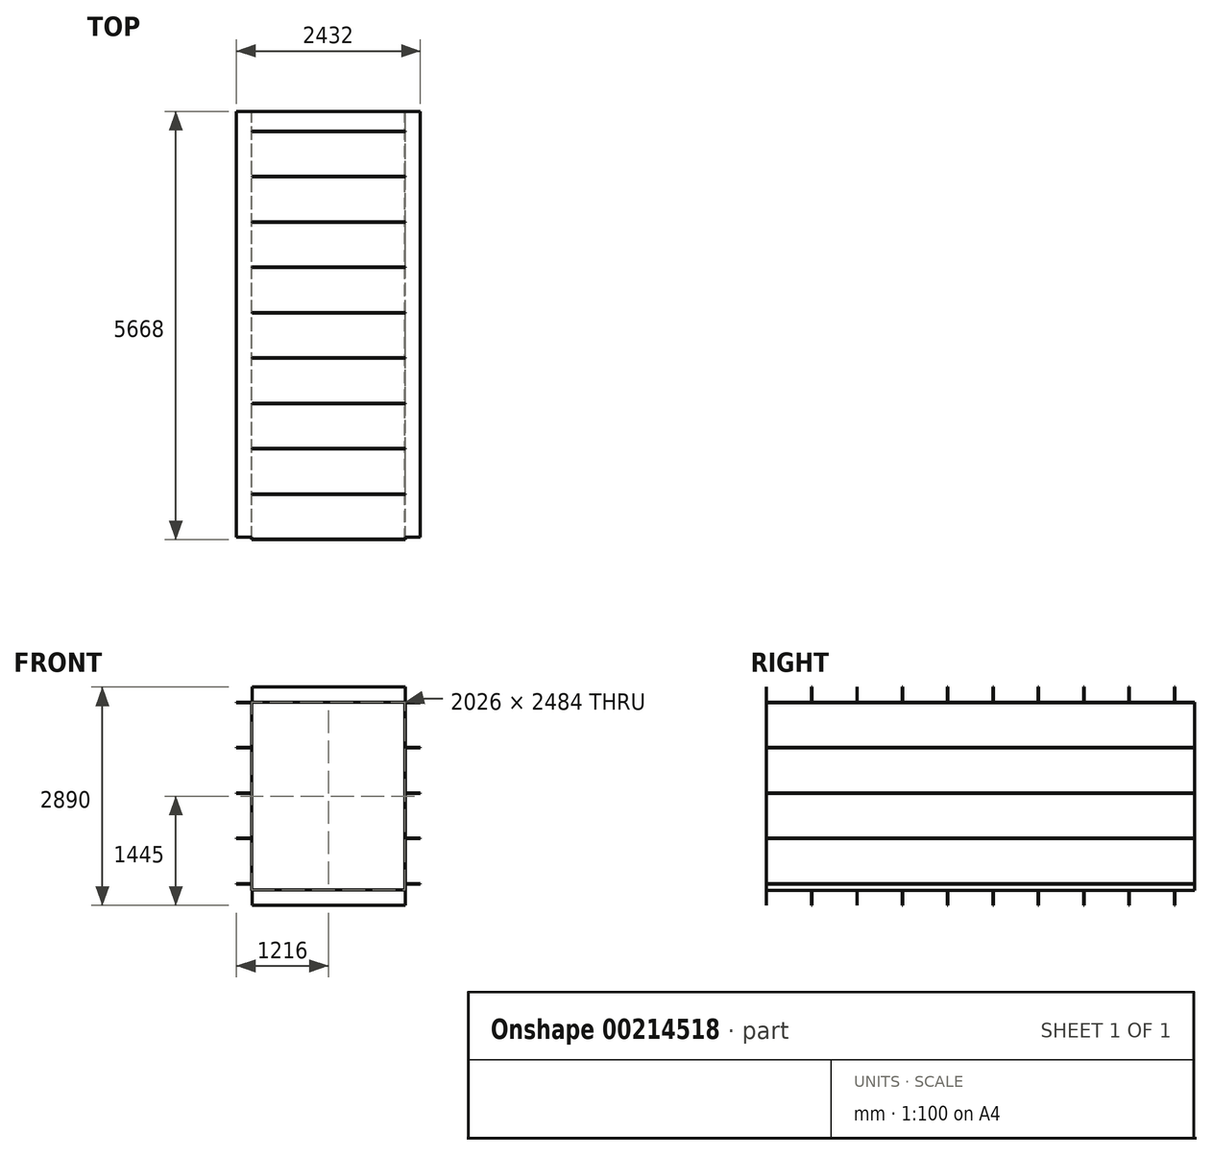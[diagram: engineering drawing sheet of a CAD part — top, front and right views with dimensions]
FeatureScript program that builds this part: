
annotation { "Feature Type Name" : "Feature", "Feature Type Description" : "" }
export const myFeature = defineFeature(function(context is Context, id is Id, definition is map)
    precondition{}
    {
        {
            var Q0;
            Q0=qCreatedBy(makeId("Front.planeOp"),FACE);
            var sketch = newSketch(context, id + "F0", { "sketchPlane" : qUnion([Q0])});
            skLineSegment(sketch, "E0.bottom", {"start": v(-1013, 1242) * mm, "end": v(1013, 1242) * mm});
            skLineSegment(sketch, "E0.top", {"start": v(-1013, -1242) * mm, "end": v(1013, -1242) * mm});
            skLineSegment(sketch, "E0.left", {"start": v(-1013, 1242) * mm, "end": v(-1013, -1242) * mm});
            skLineSegment(sketch, "E0.right", {"start": v(1013, 1242) * mm, "end": v(1013, -1242) * mm});
            skLineSegment(sketch, "E1.bottom", {"start": v(-1016, 1245) * mm, "end": v(1016, 1245) * mm});
            skLineSegment(sketch, "E1.top", {"start": v(-1016, -1245) * mm, "end": v(1016, -1245) * mm});
            skLineSegment(sketch, "E1.left", {"start": v(-1016, 1245) * mm, "end": v(-1016, -1245) * mm});
            skLineSegment(sketch, "E1.right", {"start": v(1016, 1245) * mm, "end": v(1016, -1245) * mm});
            skSolve(sketch);
        }
        {
            var Q0;
            Q0 = qSketchRegion(id + "F0", true);
            extrude(context, id + "F1", {"entities" : qUnion([Q0]), "depth" : 5668 * mm});
        }
        {
            var Q0;
            Q0=qCreatedBy(makeId("Front.planeOp"),FACE);
            var sketch = newSketch(context, id + "F2", { "sketchPlane" : qUnion([Q0])});
            skLineSegment(sketch, "E2.bottom", {"start": v(1016, 1245) * mm, "end": v(1216, 1245) * mm});
            skLineSegment(sketch, "E2.top", {"start": v(1016, 1240) * mm, "end": v(1216, 1240) * mm});
            skLineSegment(sketch, "E2.left", {"start": v(1016, 1245) * mm, "end": v(1016, 1240) * mm});
            skLineSegment(sketch, "E2.right", {"start": v(1216, 1245) * mm, "end": v(1216, 1240) * mm});
            skLineSegment(sketch, "E3.0.1.0", {"start": v(1016, 640) * mm, "end": v(1216, 640) * mm});
            skLineSegment(sketch, "E3.0.1.1", {"start": v(1016, 645) * mm, "end": v(1216, 645) * mm});
            skLineSegment(sketch, "E3.0.1.2", {"start": v(1016, 645) * mm, "end": v(1016, 640) * mm});
            skLineSegment(sketch, "E3.0.1.3", {"start": v(1216, 645) * mm, "end": v(1216, 640) * mm});
            skLineSegment(sketch, "E3.0.2.0", {"start": v(1016, 40) * mm, "end": v(1216, 40) * mm});
            skLineSegment(sketch, "E3.0.2.1", {"start": v(1016, 45) * mm, "end": v(1216, 45) * mm});
            skLineSegment(sketch, "E3.0.2.2", {"start": v(1016, 45) * mm, "end": v(1016, 40) * mm});
            skLineSegment(sketch, "E3.0.2.3", {"start": v(1216, 45) * mm, "end": v(1216, 40) * mm});
            skLineSegment(sketch, "E3.0.3.0", {"start": v(1016, -560) * mm, "end": v(1216, -560) * mm});
            skLineSegment(sketch, "E3.0.3.1", {"start": v(1016, -555) * mm, "end": v(1216, -555) * mm});
            skLineSegment(sketch, "E3.0.3.2", {"start": v(1016, -555) * mm, "end": v(1016, -560) * mm});
            skLineSegment(sketch, "E3.0.3.3", {"start": v(1216, -555) * mm, "end": v(1216, -560) * mm});
            skLineSegment(sketch, "E3.0.4.0", {"start": v(1016, -1160) * mm, "end": v(1216, -1160) * mm});
            skLineSegment(sketch, "E3.0.4.1", {"start": v(1016, -1155) * mm, "end": v(1216, -1155) * mm});
            skLineSegment(sketch, "E3.0.4.2", {"start": v(1016, -1155) * mm, "end": v(1016, -1160) * mm});
            skLineSegment(sketch, "E3.0.4.3", {"start": v(1216, -1155) * mm, "end": v(1216, -1160) * mm});
            skLineSegment(sketch, "E3.direction1", {"start": v(1016, 1240) * mm, "end": v(1044, 1240) * mm, "construction": true});
            skLineSegment(sketch, "E3.direction2", {"start": v(1016, 1240) * mm, "end": v(1016, 640) * mm, "construction": true});
            skLineSegment(sketch, "E4.bottom", {"start": v(-1016, 1245) * mm, "end": v(-1216, 1245) * mm});
            skLineSegment(sketch, "E4.top", {"start": v(-1016, 1240) * mm, "end": v(-1216, 1240) * mm});
            skLineSegment(sketch, "E4.left", {"start": v(-1016, 1245) * mm, "end": v(-1016, 1240) * mm});
            skLineSegment(sketch, "E4.right", {"start": v(-1216, 1245) * mm, "end": v(-1216, 1240) * mm});
            skLineSegment(sketch, "E5.0.1.0", {"start": v(-1016, 640) * mm, "end": v(-1216, 640) * mm});
            skLineSegment(sketch, "E5.0.1.1", {"start": v(-1016, 645) * mm, "end": v(-1216, 645) * mm});
            skLineSegment(sketch, "E5.0.1.2", {"start": v(-1016, 645) * mm, "end": v(-1016, 640) * mm});
            skLineSegment(sketch, "E5.0.1.3", {"start": v(-1216, 645) * mm, "end": v(-1216, 640) * mm});
            skLineSegment(sketch, "E5.0.2.0", {"start": v(-1016, 40) * mm, "end": v(-1216, 40) * mm});
            skLineSegment(sketch, "E5.0.2.1", {"start": v(-1016, 45) * mm, "end": v(-1216, 45) * mm});
            skLineSegment(sketch, "E5.0.2.2", {"start": v(-1016, 45) * mm, "end": v(-1016, 40) * mm});
            skLineSegment(sketch, "E5.0.2.3", {"start": v(-1216, 45) * mm, "end": v(-1216, 40) * mm});
            skLineSegment(sketch, "E5.0.3.0", {"start": v(-1016, -560) * mm, "end": v(-1216, -560) * mm});
            skLineSegment(sketch, "E5.0.3.1", {"start": v(-1016, -555) * mm, "end": v(-1216, -555) * mm});
            skLineSegment(sketch, "E5.0.3.2", {"start": v(-1016, -555) * mm, "end": v(-1016, -560) * mm});
            skLineSegment(sketch, "E5.0.3.3", {"start": v(-1216, -555) * mm, "end": v(-1216, -560) * mm});
            skLineSegment(sketch, "E5.0.4.0", {"start": v(-1016, -1160) * mm, "end": v(-1216, -1160) * mm});
            skLineSegment(sketch, "E5.0.4.1", {"start": v(-1016, -1155) * mm, "end": v(-1216, -1155) * mm});
            skLineSegment(sketch, "E5.0.4.2", {"start": v(-1016, -1155) * mm, "end": v(-1016, -1160) * mm});
            skLineSegment(sketch, "E5.0.4.3", {"start": v(-1216, -1155) * mm, "end": v(-1216, -1160) * mm});
            skLineSegment(sketch, "E5.direction1", {"start": v(-1216, 1240) * mm, "end": v(-1191, 1240) * mm, "construction": true});
            skLineSegment(sketch, "E5.direction2", {"start": v(-1216, 1240) * mm, "end": v(-1216, 640) * mm, "construction": true});
            skSolve(sketch);
        }
        {
            var Q0;
            Q0 = qSketchRegion(id + "F2", true);
            extrude(context, id + "F3", {"entities" : qUnion([Q0]), "operationType" : NewBodyOperationType.ADD, "depth" : 5638 * mm});
        }
        {
            var Q0;
            Q0=makeQuery(id+"F1.opExtrude","SWEPT_FACE",FACE,{"disambiguationData":[OSD([sQuery(id+"F0.wireOp",EDGE,"E1.right")])]});
            var sketch = newSketch(context, id + "F4", { "sketchPlane" : qUnion([Q0])});
            skLineSegment(sketch, "E6.bottom", {"start": v(-5668, 1245) * mm, "end": v(-5663, 1245) * mm});
            skLineSegment(sketch, "E6.top", {"start": v(-5668, 1445) * mm, "end": v(-5663, 1445) * mm});
            skLineSegment(sketch, "E6.left", {"start": v(-5668, 1245) * mm, "end": v(-5668, 1445) * mm});
            skLineSegment(sketch, "E6.right", {"start": v(-5663, 1245) * mm, "end": v(-5663, 1445) * mm});
            skLineSegment(sketch, "E7.1.0.0", {"start": v(-5068, 1245) * mm, "end": v(-5068, 1445) * mm});
            skLineSegment(sketch, "E7.1.0.1", {"start": v(-5063, 1245) * mm, "end": v(-5063, 1445) * mm});
            skLineSegment(sketch, "E7.1.0.2", {"start": v(-5068, 1245) * mm, "end": v(-5063, 1245) * mm});
            skLineSegment(sketch, "E7.1.0.3", {"start": v(-5068, 1445) * mm, "end": v(-5063, 1445) * mm});
            skLineSegment(sketch, "E7.2.0.0", {"start": v(-4468, 1245) * mm, "end": v(-4468, 1445) * mm});
            skLineSegment(sketch, "E7.2.0.1", {"start": v(-4463, 1245) * mm, "end": v(-4463, 1445) * mm});
            skLineSegment(sketch, "E7.2.0.2", {"start": v(-4468, 1245) * mm, "end": v(-4463, 1245) * mm});
            skLineSegment(sketch, "E7.2.0.3", {"start": v(-4468, 1445) * mm, "end": v(-4463, 1445) * mm});
            skLineSegment(sketch, "E7.3.0.0", {"start": v(-3868, 1245) * mm, "end": v(-3868, 1445) * mm});
            skLineSegment(sketch, "E7.3.0.1", {"start": v(-3863, 1245) * mm, "end": v(-3863, 1445) * mm});
            skLineSegment(sketch, "E7.3.0.2", {"start": v(-3868, 1245) * mm, "end": v(-3863, 1245) * mm});
            skLineSegment(sketch, "E7.3.0.3", {"start": v(-3868, 1445) * mm, "end": v(-3863, 1445) * mm});
            skLineSegment(sketch, "E7.4.0.0", {"start": v(-3268, 1245) * mm, "end": v(-3268, 1445) * mm});
            skLineSegment(sketch, "E7.4.0.1", {"start": v(-3263, 1245) * mm, "end": v(-3263, 1445) * mm});
            skLineSegment(sketch, "E7.4.0.2", {"start": v(-3268, 1245) * mm, "end": v(-3263, 1245) * mm});
            skLineSegment(sketch, "E7.4.0.3", {"start": v(-3268, 1445) * mm, "end": v(-3263, 1445) * mm});
            skLineSegment(sketch, "E7.5.0.0", {"start": v(-2668, 1245) * mm, "end": v(-2668, 1445) * mm});
            skLineSegment(sketch, "E7.5.0.1", {"start": v(-2663, 1245) * mm, "end": v(-2663, 1445) * mm});
            skLineSegment(sketch, "E7.5.0.2", {"start": v(-2668, 1245) * mm, "end": v(-2663, 1245) * mm});
            skLineSegment(sketch, "E7.5.0.3", {"start": v(-2668, 1445) * mm, "end": v(-2663, 1445) * mm});
            skLineSegment(sketch, "E7.6.0.0", {"start": v(-2068, 1245) * mm, "end": v(-2068, 1445) * mm});
            skLineSegment(sketch, "E7.6.0.1", {"start": v(-2063, 1245) * mm, "end": v(-2063, 1445) * mm});
            skLineSegment(sketch, "E7.6.0.2", {"start": v(-2068, 1245) * mm, "end": v(-2063, 1245) * mm});
            skLineSegment(sketch, "E7.6.0.3", {"start": v(-2068, 1445) * mm, "end": v(-2063, 1445) * mm});
            skLineSegment(sketch, "E7.7.0.0", {"start": v(-1468, 1245) * mm, "end": v(-1468, 1445) * mm});
            skLineSegment(sketch, "E7.7.0.1", {"start": v(-1463, 1245) * mm, "end": v(-1463, 1445) * mm});
            skLineSegment(sketch, "E7.7.0.2", {"start": v(-1468, 1245) * mm, "end": v(-1463, 1245) * mm});
            skLineSegment(sketch, "E7.7.0.3", {"start": v(-1468, 1445) * mm, "end": v(-1463, 1445) * mm});
            skLineSegment(sketch, "E7.8.0.0", {"start": v(-868, 1245) * mm, "end": v(-868, 1445) * mm});
            skLineSegment(sketch, "E7.8.0.1", {"start": v(-863, 1245) * mm, "end": v(-863, 1445) * mm});
            skLineSegment(sketch, "E7.8.0.2", {"start": v(-868, 1245) * mm, "end": v(-863, 1245) * mm});
            skLineSegment(sketch, "E7.8.0.3", {"start": v(-868, 1445) * mm, "end": v(-863, 1445) * mm});
            skLineSegment(sketch, "E7.9.0.0", {"start": v(-268, 1245) * mm, "end": v(-268, 1445) * mm});
            skLineSegment(sketch, "E7.9.0.1", {"start": v(-263, 1245) * mm, "end": v(-263, 1445) * mm});
            skLineSegment(sketch, "E7.9.0.2", {"start": v(-268, 1245) * mm, "end": v(-263, 1245) * mm});
            skLineSegment(sketch, "E7.9.0.3", {"start": v(-268, 1445) * mm, "end": v(-263, 1445) * mm});
            skLineSegment(sketch, "E7.direction1", {"start": v(-5668, 1245) * mm, "end": v(-5068, 1245) * mm, "construction": true});
            skLineSegment(sketch, "E8.bottom", {"start": v(-5668, -1245) * mm, "end": v(-5663, -1245) * mm});
            skLineSegment(sketch, "E8.top", {"start": v(-5668, -1445) * mm, "end": v(-5663, -1445) * mm});
            skLineSegment(sketch, "E8.left", {"start": v(-5668, -1245) * mm, "end": v(-5668, -1445) * mm});
            skLineSegment(sketch, "E8.right", {"start": v(-5663, -1245) * mm, "end": v(-5663, -1445) * mm});
            skLineSegment(sketch, "E9.1.0.0", {"start": v(-5063, -1245) * mm, "end": v(-5063, -1445) * mm});
            skLineSegment(sketch, "E9.1.0.1", {"start": v(-5068, -1245) * mm, "end": v(-5068, -1445) * mm});
            skLineSegment(sketch, "E9.1.0.2", {"start": v(-5068, -1245) * mm, "end": v(-5063, -1245) * mm});
            skLineSegment(sketch, "E9.1.0.3", {"start": v(-5068, -1445) * mm, "end": v(-5063, -1445) * mm});
            skLineSegment(sketch, "E9.2.0.0", {"start": v(-4463, -1245) * mm, "end": v(-4463, -1445) * mm});
            skLineSegment(sketch, "E9.2.0.1", {"start": v(-4468, -1245) * mm, "end": v(-4468, -1445) * mm});
            skLineSegment(sketch, "E9.2.0.2", {"start": v(-4468, -1245) * mm, "end": v(-4463, -1245) * mm});
            skLineSegment(sketch, "E9.2.0.3", {"start": v(-4468, -1445) * mm, "end": v(-4463, -1445) * mm});
            skLineSegment(sketch, "E9.3.0.0", {"start": v(-3863, -1245) * mm, "end": v(-3863, -1445) * mm});
            skLineSegment(sketch, "E9.3.0.1", {"start": v(-3868, -1245) * mm, "end": v(-3868, -1445) * mm});
            skLineSegment(sketch, "E9.3.0.2", {"start": v(-3868, -1245) * mm, "end": v(-3863, -1245) * mm});
            skLineSegment(sketch, "E9.3.0.3", {"start": v(-3868, -1445) * mm, "end": v(-3863, -1445) * mm});
            skLineSegment(sketch, "E9.4.0.0", {"start": v(-3263, -1245) * mm, "end": v(-3263, -1445) * mm});
            skLineSegment(sketch, "E9.4.0.1", {"start": v(-3268, -1245) * mm, "end": v(-3268, -1445) * mm});
            skLineSegment(sketch, "E9.4.0.2", {"start": v(-3268, -1245) * mm, "end": v(-3263, -1245) * mm});
            skLineSegment(sketch, "E9.4.0.3", {"start": v(-3268, -1445) * mm, "end": v(-3263, -1445) * mm});
            skLineSegment(sketch, "E9.5.0.0", {"start": v(-2663, -1245) * mm, "end": v(-2663, -1445) * mm});
            skLineSegment(sketch, "E9.5.0.1", {"start": v(-2668, -1245) * mm, "end": v(-2668, -1445) * mm});
            skLineSegment(sketch, "E9.5.0.2", {"start": v(-2668, -1245) * mm, "end": v(-2663, -1245) * mm});
            skLineSegment(sketch, "E9.5.0.3", {"start": v(-2668, -1445) * mm, "end": v(-2663, -1445) * mm});
            skLineSegment(sketch, "E9.6.0.0", {"start": v(-2063, -1245) * mm, "end": v(-2063, -1445) * mm});
            skLineSegment(sketch, "E9.6.0.1", {"start": v(-2068, -1245) * mm, "end": v(-2068, -1445) * mm});
            skLineSegment(sketch, "E9.6.0.2", {"start": v(-2068, -1245) * mm, "end": v(-2063, -1245) * mm});
            skLineSegment(sketch, "E9.6.0.3", {"start": v(-2068, -1445) * mm, "end": v(-2063, -1445) * mm});
            skLineSegment(sketch, "E9.7.0.0", {"start": v(-1463, -1245) * mm, "end": v(-1463, -1445) * mm});
            skLineSegment(sketch, "E9.7.0.1", {"start": v(-1468, -1245) * mm, "end": v(-1468, -1445) * mm});
            skLineSegment(sketch, "E9.7.0.2", {"start": v(-1468, -1245) * mm, "end": v(-1463, -1245) * mm});
            skLineSegment(sketch, "E9.7.0.3", {"start": v(-1468, -1445) * mm, "end": v(-1463, -1445) * mm});
            skLineSegment(sketch, "E9.8.0.0", {"start": v(-863, -1245) * mm, "end": v(-863, -1445) * mm});
            skLineSegment(sketch, "E9.8.0.1", {"start": v(-868, -1245) * mm, "end": v(-868, -1445) * mm});
            skLineSegment(sketch, "E9.8.0.2", {"start": v(-868, -1245) * mm, "end": v(-863, -1245) * mm});
            skLineSegment(sketch, "E9.8.0.3", {"start": v(-868, -1445) * mm, "end": v(-863, -1445) * mm});
            skLineSegment(sketch, "E9.9.0.0", {"start": v(-263, -1245) * mm, "end": v(-263, -1445) * mm});
            skLineSegment(sketch, "E9.9.0.1", {"start": v(-268, -1245) * mm, "end": v(-268, -1445) * mm});
            skLineSegment(sketch, "E9.9.0.2", {"start": v(-268, -1245) * mm, "end": v(-263, -1245) * mm});
            skLineSegment(sketch, "E9.9.0.3", {"start": v(-268, -1445) * mm, "end": v(-263, -1445) * mm});
            skLineSegment(sketch, "E9.direction1", {"start": v(-5668, -1445) * mm, "end": v(-5068, -1445) * mm, "construction": true});
            skSolve(sketch);
        }
        {
            var Q0;
            Q0 = qSketchRegion(id + "F4", true);
            extrude(context, id + "F5", {"entities" : qUnion([Q0]), "operationType" : NewBodyOperationType.ADD, "oppositeDirection" : true, "depth" : 2026 * mm});
        }
    });
